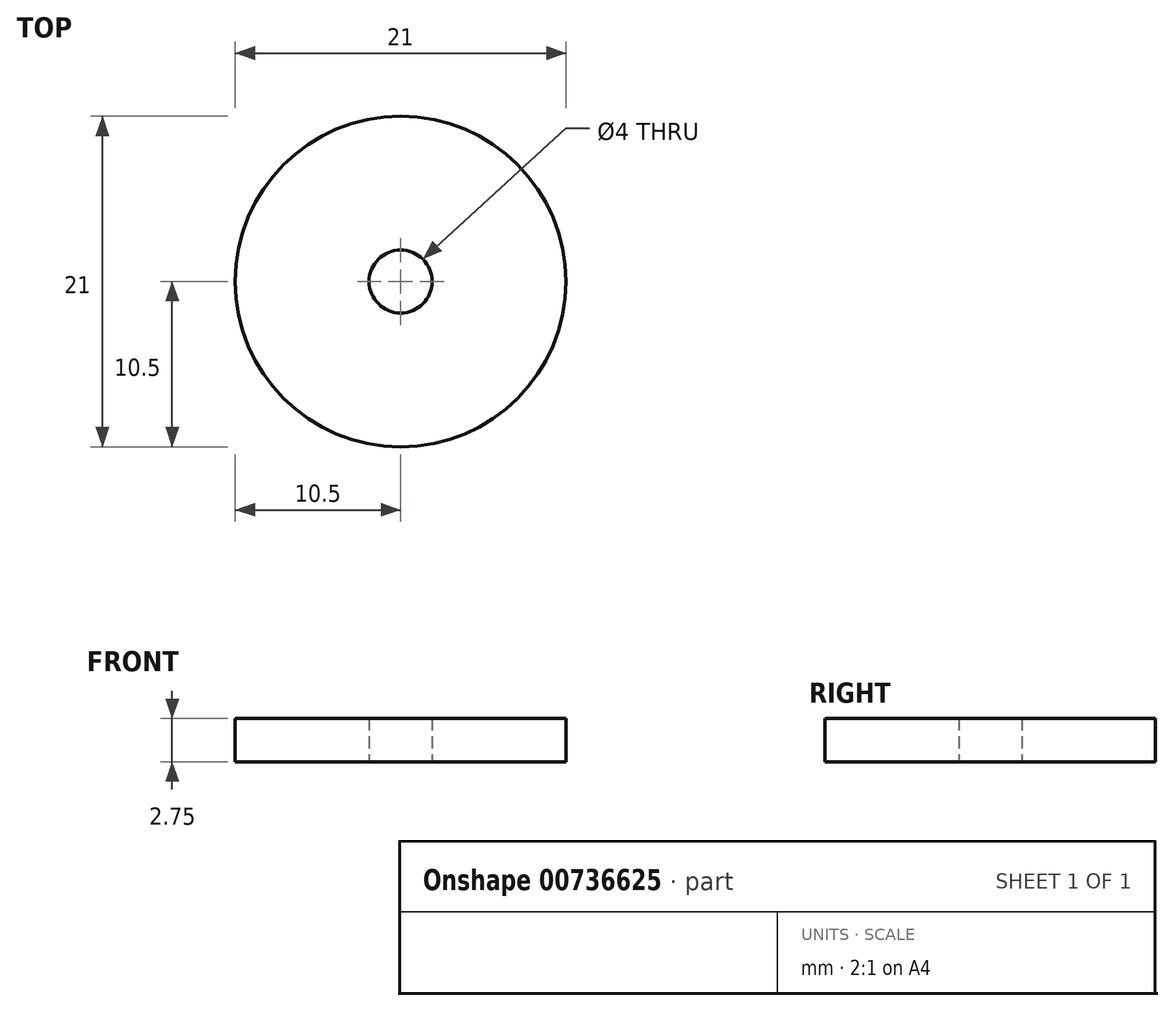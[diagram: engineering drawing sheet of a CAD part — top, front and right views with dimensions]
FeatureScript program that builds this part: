
annotation { "Feature Type Name" : "Feature", "Feature Type Description" : "" }
export const myFeature = defineFeature(function(context is Context, id is Id, definition is map)
    precondition{}
    {
        {
            var Q0;
            Q0=qCreatedBy(makeId("Top.planeOp"),FACE);
            var sketch = newSketch(context, id + "F0", { "sketchPlane" : qUnion([Q0])});
            skCircle(sketch, "E0", {"center": v(0, 0) * mm, "radius": 10.5 * mm});
            skCircle(sketch, "E1", {"center": v(0, 0) * mm, "radius": 2 * mm});
            skSolve(sketch);
        }
        {
            var Q0;
            Q0 = qSketchRegion(id + "F0", true);
            extrude(context, id + "F1", {"entities" : qUnion([Q0]), "depth" : 2.75 * mm, "offsetDistance" : 25 * mm});
        }
    });
